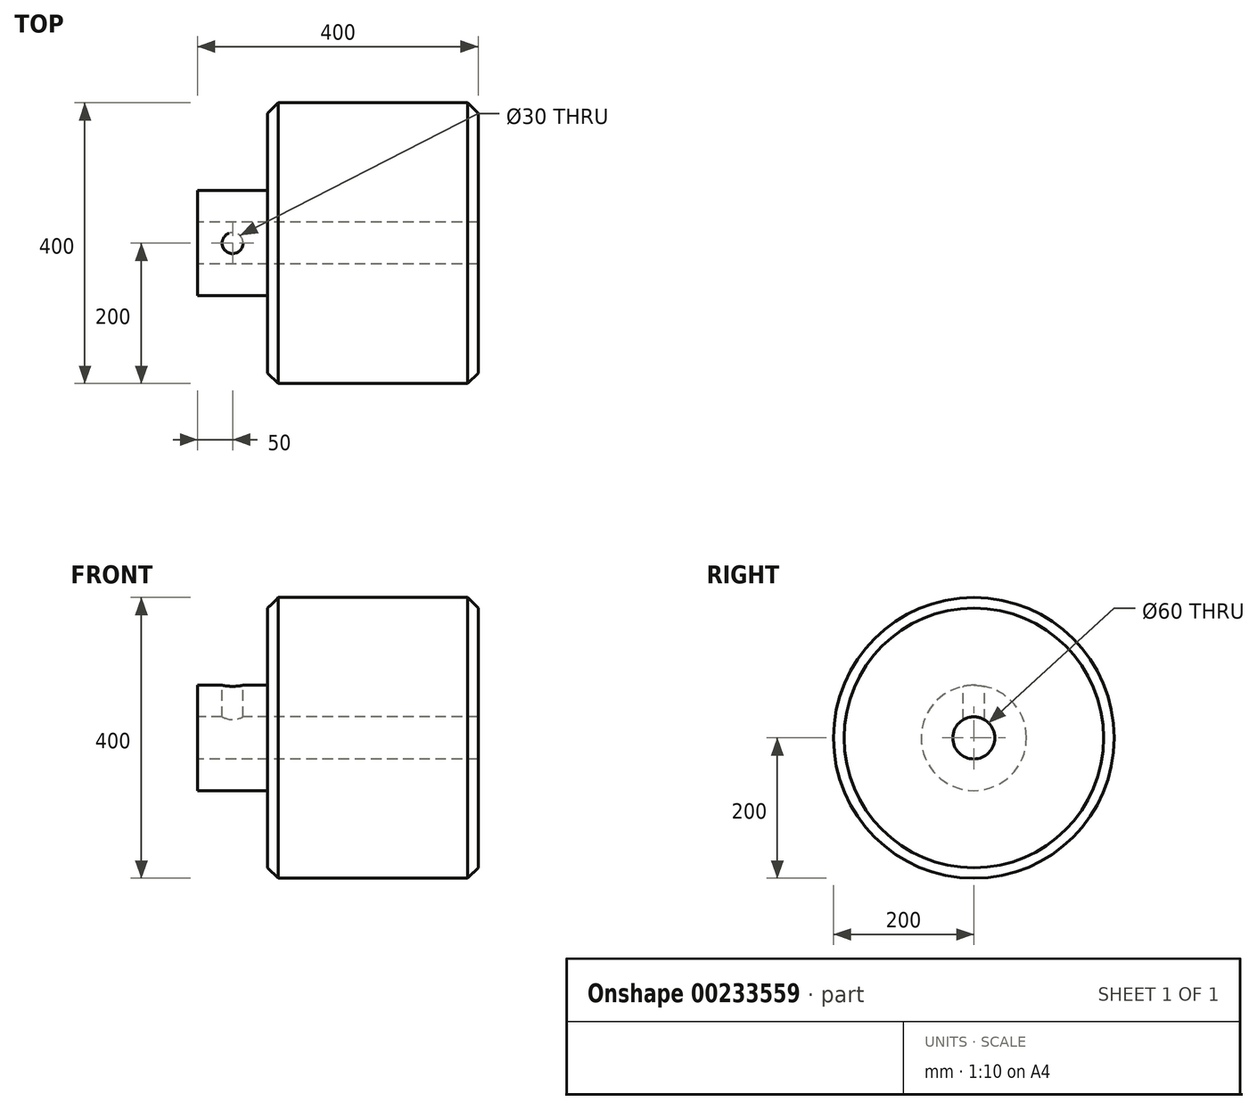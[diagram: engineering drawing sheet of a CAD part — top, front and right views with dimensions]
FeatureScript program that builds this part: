
annotation { "Feature Type Name" : "Feature", "Feature Type Description" : "" }
export const myFeature = defineFeature(function(context is Context, id is Id, definition is map)
    precondition{}
    {
        {
            var Q0;
            Q0=qCreatedBy(makeId("Front.planeOp"),FACE);
            var sketch = newSketch(context, id + "F0", { "sketchPlane" : qUnion([Q0])});
            skLineSegment(sketch, "E0", {"start": v(200, 30) * mm, "end": v(-200, 30) * mm});
            skLineSegment(sketch, "E1", {"start": v(-200, 30) * mm, "end": v(-200, 75) * mm});
            skLineSegment(sketch, "E2", {"start": v(-200, 75) * mm, "end": v(-100, 75) * mm});
            skLineSegment(sketch, "E3", {"start": v(-100, 75) * mm, "end": v(-100, 200) * mm});
            skLineSegment(sketch, "E4", {"start": v(-100, 200) * mm, "end": v(200, 200) * mm});
            skLineSegment(sketch, "E5", {"start": v(200, 200) * mm, "end": v(200, 30) * mm});
            skPoint(sketch, "E6", {"position": v(-150, 75) * mm});
            skLineSegment(sketch, "E7", {"start": v(-291.86, 0) * mm, "end": v(320.28, 0) * mm, "construction": true});
            skSolve(sketch);
        }
        {
            var Q0;
            Q0=makeQuery(id+"F0.imprint","IMPRINT",FACE,{"disambiguationData":[TD([[makeQuery(id+"F0.imprint","IMPRINT",EDGE,{"derivedFrom":sQuery(id+"F0.wireOp",EDGE,"E0")}),-1.0]])]});
            var Q1;
            Q1=sQuery(id+"F0.wireOp",EDGE,"E7");
            revolve(context, id + "F1", {"entities" : qUnion([Q0]), "axis" : qUnion([Q1]), "revolveType" : RevolveType.FULL});
        }
        {
            var Q0;
            Q0=makeQuery(id+"F1.opRevolve","SWEPT_EDGE",EDGE,{"disambiguationData":[OSD([sQuery(id+"F0.wireOp",EDGE,"E3"),sQuery(id+"F0.wireOp",EDGE,"E4")])]});
            var Q1;
            Q1=makeQuery(id+"F1.opRevolve","SWEPT_EDGE",EDGE,{"disambiguationData":[OSD([sQuery(id+"F0.wireOp",EDGE,"E4"),sQuery(id+"F0.wireOp",EDGE,"E5")])]});
            chamfer(context, id + "F2", {"entities" : qUnion([Q0, Q1]), "chamferType" : ChamferType.OFFSET_ANGLE, "width" : 15 * mm, "oppositeDirection" : false, "angle" : 45 * degree, "tangentPropagation" : true});
        }
        {
            var Q0;
            Q0=qCreatedBy(makeId("Top.planeOp"),FACE);
            cPlane(context, id + "F3", {"entities" : qUnion([Q0]), "cplaneType" : CPlaneType.OFFSET, "offset" : 75 * mm, "width" : 150 * mm, "height" : 150 * mm});
        }
        {
            var Q0;
            Q0=qCreatedBy(id+"F3.planeOp",FACE);
            var sketch = newSketch(context, id + "F4", { "sketchPlane" : qUnion([Q0])});
            skCircle(sketch, "E8", {"center": v(-150, 0) * mm, "radius": 15 * mm, "construction": true});
            skSolve(sketch);
        }
        {
            var Q0;
            Q0=sQuery(id+"F4.wireOp",VERTEX,"E8.center");
            var Q1;
            Q1=makeQuery(id+"F1.opRevolve","SWEPT_BODY",BODY,{"disambiguationData":[OSD([sQuery(id+"F0.wireOp",EDGE,"E0"),sQuery(id+"F0.wireOp",EDGE,"E1"),sQuery(id+"F0.wireOp",EDGE,"E2"),sQuery(id+"F0.wireOp",EDGE,"E3"),sQuery(id+"F0.wireOp",EDGE,"E4"),sQuery(id+"F0.wireOp",EDGE,"E5")])]});
            hole(context, id + "F5", {"style" : HoleStyle.SIMPLE, "endStyle" : HoleEndStyle.BLIND, "holeDiameter" : 30 * mm, "holeDepth" : 75 * mm, "startFromSketch" : true, "locations" : qUnion([Q0]), "scope" : qUnion([Q1])});
        }
    });
